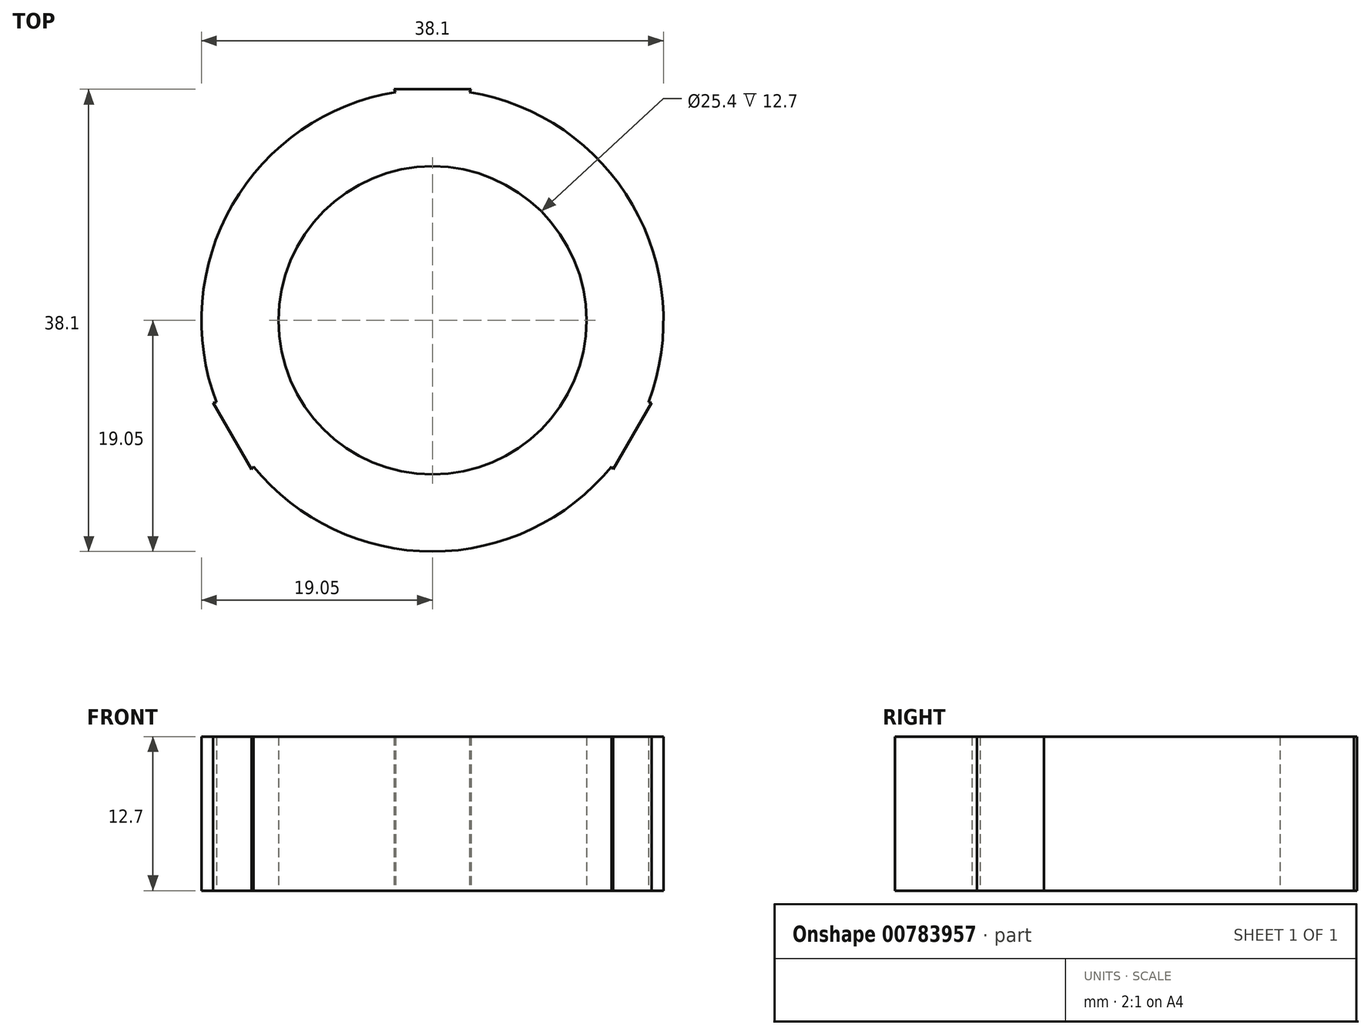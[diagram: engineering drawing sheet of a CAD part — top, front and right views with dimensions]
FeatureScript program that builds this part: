
annotation { "Feature Type Name" : "Feature", "Feature Type Description" : "" }
export const myFeature = defineFeature(function(context is Context, id is Id, definition is map)
    precondition{}
    {
        {
            var Q0;
            Q0=qCreatedBy(makeId("Top.planeOp"),FACE);
            var sketch = newSketch(context, id + "F0", { "sketchPlane" : qUnion([Q0])});
            skCircle(sketch, "E0", {"center": v(0, 0) * mm, "radius": 12.7 * mm});
            skCircle(sketch, "E1", {"center": v(0, 0) * mm, "radius": 19.05 * mm});
            skLineSegment(sketch, "E2", {"start": v(0, 19.05) * mm, "end": v(0, 12.7) * mm});
            skLineSegment(sketch, "E3", {"start": v(-16.5, -9.53) * mm, "end": v(-11, -6.35) * mm});
            skLineSegment(sketch, "E4", {"start": v(16.5, -9.53) * mm, "end": v(11, -6.35) * mm});
            skLineSegment(sketch, "E5", {"start": v(-16.5, -9.53) * mm, "end": v(-18.09, -6.78) * mm});
            skLineSegment(sketch, "E6", {"start": v(-16.5, -9.53) * mm, "end": v(-14.91, -12.27) * mm});
            skLineSegment(sketch, "E7", {"start": v(-14.91, -12.27) * mm, "end": v(-11, -6.35) * mm});
            skLineSegment(sketch, "E8", {"start": v(-11, -6.35) * mm, "end": v(-18.09, -6.78) * mm});
            skLineSegment(sketch, "E9", {"start": v(0, 19.05) * mm, "end": v(-3.18, 19.05) * mm});
            skLineSegment(sketch, "E10", {"start": v(0, 19.05) * mm, "end": v(3.18, 19.05) * mm});
            skLineSegment(sketch, "E11", {"start": v(-3.18, 19.05) * mm, "end": v(0, 12.7) * mm});
            skLineSegment(sketch, "E12", {"start": v(0, 12.7) * mm, "end": v(3.18, 19.05) * mm});
            skLineSegment(sketch, "E13", {"start": v(16.5, -9.53) * mm, "end": v(18.09, -6.78) * mm});
            skLineSegment(sketch, "E14", {"start": v(16.5, -9.53) * mm, "end": v(14.91, -12.27) * mm});
            skLineSegment(sketch, "E15", {"start": v(14.91, -12.27) * mm, "end": v(11, -6.35) * mm});
            skLineSegment(sketch, "E16", {"start": v(11, -6.35) * mm, "end": v(18.09, -6.78) * mm});
            skSolve(sketch);
        }
        {
            var Q0;
            Q0 = qSketchRegion(id + "F0", true);
            extrude(context, id + "F1", {"entities" : qUnion([Q0]), "depth" : 12.7 * mm, "offsetDistance" : 25.4 * mm});
        }
    });
